# Revit family: Sanitary_Compound-Units_hansgrohe_54000CHN-CubeStack-Vanity-unit-for-furni_1
name_source: partatom
category: Furniture
revit_build: Autodesk Revit 2018 (Build: 20170223_1515(x64)
units: mm (PartAtom-declared; Revit-internal decimal feet)

## family parameters
Always vertical = No
Cut with Voids When Loaded = No
OmniClass Number = 23.40.00.00
OmniClass Title = Equipment and Furnishings
Room Calculation Point = No
Shared = No
Work Plane-Based = Yes

## types (1)
- 477 Agategrey
    Always visible = Yes
    BIMobject category = Compound Units
    Default Elevation = 1219.2 mm  [stored 4 ft]
    Description = CubeStack Vanity unit for furniture washbasin 800/500
    Design country = Germany
    EAN code = 4059625328453
    Edition number = 1
    GTIN code = https://4059625328453
    IFC Classification = Furnishing Element
    Manufacturer = hansgrohe
    Manufacturer country = Germany
    Manufacturer name = hansgrohe
    Masterformat 2014 Code = 12 35 30.23
    Masterformat 2014 Description = Bathroom Casework
    Material 1 = Hansgrohe - Wood - 477 Agategrey
    Model = 54000CHN
    NBS Reference Code = 35-75-94
    NBS Reference Description = Vanity Units
    OmniClass Code = 23-21 19 15 33 13
    OmniClass Description = Residential Bathroom Specialty Casework
    Product Guid = 9769950d-ff22-4518-a11c-309064f92607
    Product SKU = 54000CHN
    Product data url = https://bimobject.com
    Product family = CubeStack
    Product group = vanity unit
    Product name = 54000CHN CubeStack Vanity unit for furniture washbasin 800/500
    QR code = https://bimobject.com
    URL = https://www.hansgrohe.com
https://www.hansgrohe.com
    Uniclass 2015 Code = Pr_40_20_76_94
    Uniclass 2015 Name = Vanity units
    Uniformat II Code = E2010
    Uniformat II Description = Fixed Furnishings
    Weight Net (Kg) = 58

note: [stored X ft] marks values corroborated as IEEE doubles in the binary element streams (Revit-internal decimal feet)

## geometry (parser evidence)
native form markers: Sweep x3
no freeform markers — native parametric forms only
